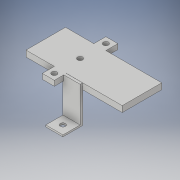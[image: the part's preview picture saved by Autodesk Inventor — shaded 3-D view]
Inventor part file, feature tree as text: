
AUTODESK INVENTOR PART (.ipt)
format: ipt  version: 2018 (Build 220112000, 112)  size: 195,072 bytes
history: native  units: in
note: dims shown in document units (in); Inventor stores cm internally (conversion verified against a paired STEP export)
features: extrude x9, sketch x9
ambient origin geometry x8: Origin, YZ Plane, XZ Plane, XY Plane, X Axis, Y Axis, Z Axis, Center Point
bodies: Solid1 (feature_tree)
feature tree (18):
  extrude  "Extrusion1"  Depth=0.3937in
  extrude  "Extrusion2"  Depth=0.0394in TaperAngle=0.0deg
  extrude  "Extrusion3"  Depth=0.0394in TaperAngle=0.0deg
  extrude  "Extrusion4"  Depth=0.6693in TaperAngle=0.0deg
  extrude  "Extrusion5"  TaperAngle=0.0deg  [1 undecoded]
  extrude  "Extrusion6"  Depth=2.2047in
  extrude  "Extrusion7"  Depth=0.9055in
  extrude  "Extrusion8"  Depth=0.0787in TaperAngle=0.0deg
  extrude  "Extrusion9"  Depth=0.2756in
  sketch  "Sketch1"  dims[d0=0.3937in d1=0.3937in]
  sketch  "Sketch2"  dims[d2=0.1181in d3=0.0394in d4=0.0in]
  sketch  "Sketch3"  dims[d5=0.0591in d6=0.0394in d7=0.0in]
  sketch  "Sketch4"  dims[d8=0.0591in d9=0.6693in d10=0.0in]
  sketch  "Sketch5"  dims[d11=0.0591in d12=0.0in d13=0.0in]
  sketch  "Sketch6"  dims[d14=0.0591in d15=2.2047in]
  sketch  "Sketch8"  dims[d16=0.9055in d17=0.0in d18=0.7874in]
  sketch  "Sketch9"  dims[d19=0.1181in d20=0.0787in d21=0.0in]
  sketch  "Sketch10"  dims[d27=0.1181in d28=0.0in d29=0.7874in d30=0.0in d31=0.2756in d32=0.2756in d33=0.0in d34=0.2756in d35=0.2756in d36=0.1181in d37=0.1181in d38=0.0787in d39=0.0in d40=0.2756in d41=0.0in]
note: 1 required parameter value undecoded (feature->parameter linkage not recoverable at this tier; creation-order binding heuristic only, values carry confidence <= 0.55)
